# Revit family: E-312
name_source: partatom
category: Aparatos sanitarios
units: mm (PartAtom-declared; Revit-internal decimal feet)

## family parameters
Activar corte en vistas = No
Compartido = Sí
Corte con vacíos al cargar = No
Cota de conector redondo = Usar diámetro
Mantener orientación de anotación = No
Número OmniClass = 23.45.55.17
Punto de cálculo de habitación = Sí
Se basa en plano de trabajo = No
Siempre vertical = Sí
Tipo de pieza = Normal
Título OmniClass = Mixing Faucets

## types (1)
- E-312
    Comentarios de tipo = Monomando para fregadero Adara. Acabado cromo. Presión mínima requerida 1.00 kg/cm². Cabezal retráctil con dos tipos de chorro: Aereado y Spray. Cuello giratorio. Incluye juego de cubretaladros.
    Descripción = Monomando para fregadero
    Elevación por defecto = 35"
    Fabricante = HELVEX S.A. de C.V.
    Imagen de tipo = E-312.png
    Inlet Threads = ½" - 14 NPSM
    Latón = Chrome - Polished
    Max. Working Pressure = 85.3 psi
    Min. Working Pressure = 14.2 psi
    Modelo = E-312
    Support Base Diameter = 2"
    Total Height = 17"
    Total Length = 9"
    Total Width = 4"
    URL = https://helvex.com.mx

## geometry (parser evidence)
native form markers: Sweep x3
no freeform markers — native parametric forms only
